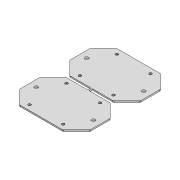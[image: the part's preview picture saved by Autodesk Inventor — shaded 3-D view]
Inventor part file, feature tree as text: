
AUTODESK INVENTOR PART (.ipt)
format: ipt  version: 2020 (Build 240168000, 168)  size: 167,424 bytes
history: native  units: mm
features: other x4, projected_geometry x2, extrude x1, sketch x1
ambient origin geometry x8: Origin, YZ Plane, XZ Plane, XY Plane, X Axis, Y Axis, Z Axis, Center Point
bodies: Body1 (feature_tree)
feature tree (8):
  other  "CCM_Base_Mount.iam"
  other  "CCM_Mount_C.ipt:1"
  other  "CCM_Mount_C.ipt:2"
  other  "ソリッド1"
  extrude  "押し出し1"  Depth=10.0mm
  sketch  "スケッチ1"
  projected_geometry  "投影ループ1"
  projected_geometry  "投影ループ2"
